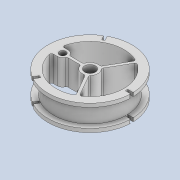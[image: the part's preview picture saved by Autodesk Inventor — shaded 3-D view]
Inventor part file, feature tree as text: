
AUTODESK INVENTOR PART (.ipt)
format: ipt  version: 2020 (Build 240168000, 168)  size: 397,312 bytes
history: native  units: mm
features: extrude x6, sketch x6, fillet x4, projected_geometry x4, pattern_circular x1, thicken_offset x1
ambient origin geometry x8: Origin, YZ Plane, XZ Plane, XY Plane, X Axis, Y Axis, Z Axis, Center Point
bodies: Solid1 (feature_tree)
feature tree (22):
  extrude  "Extrusion1"  Depth=3.0mm
  extrude  "Extrusion2"  Depth=0.7mm
  extrude  "Extrusion3"  Depth=0.7mm
  extrude  "Extrusion4"  Depth=7.5mm
  extrude  "Extrusion5"  Depth=7.0mm TaperAngle=0.0deg
  pattern_circular  "Circular Pattern1"  [2 undecoded]
  fillet  "Fillet1"  Radius=1.5mm
  fillet  "Fillet2"  Radius=1.0mm
  extrude  "Extrusion6"  Depth=0.5mm TaperAngle=0.0deg
  fillet  "Fillet3"  [1 undecoded]
  fillet  "Fillet4"  Radius=3.0mm
  thicken_offset  "Thicken1"
  sketch  "Sketch1"  dims[d0=20.0mm d1=3.0mm]
  sketch  "Sketch2"  dims[d2=0.7mm d3=0.7mm]
  projected_geometry  "Projected Loop1"
  sketch  "Sketch3"  dims[d4=5.0mm d5=0.7mm]
  projected_geometry  "Projected Loop2"
  sketch  "Sketch4"  dims[d6=30.0mm d8=360.0deg d10=7.5mm]
  projected_geometry  "Projected Loop3"
  sketch  "Sketch5"  dims[d11=3.0mm d12=7.0mm d13=0.0mm]
  projected_geometry  "Projected Loop4"
  sketch  "Sketch6"  dims[d14=1.8mm d15=19.5mm d16=0.0mm d17=1.5mm d18=1.0mm d19=0.0mm d20=1.0mm d21=0.0mm d22=60.0deg d23=3.0mm d24=0.7mm d25=20.0mm d26=0.0mm d27=30.0mm d28=360.0deg d30=0.2mm d31=0.5mm d32=5.5mm d33=2.0mm d34=0.0mm d35=0.5mm d36=0.5mm d37=1.0mm d38=1.0mm]
note: 3 required parameter values undecoded (feature->parameter linkage not recoverable at this tier; creation-order binding heuristic only, values carry confidence <= 0.55)
